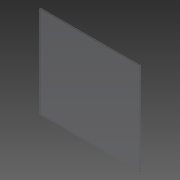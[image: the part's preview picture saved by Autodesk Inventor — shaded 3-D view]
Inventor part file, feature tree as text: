
AUTODESK INVENTOR PART (.ipt)
format: ipt  version: 2013 (Build 170138000, 138)  size: 145,920 bytes
history: native  units: in
note: dims shown in document units (in); Inventor stores cm internally (conversion verified against a paired STEP export)
features: sheet_metal_op x7, other x4, sketch x3
ambient origin geometry x8: Origin, YZ Plane, XZ Plane, XY Plane, X Axis, Y Axis, Z Axis, Center Point
bodies: Solid1 (feature_tree)
feature tree (14):
  sheet_metal_op  "Face1"
  sheet_metal_op  "Flange1"
  sheet_metal_op  "Flange2"
  sketch  "Sketch1"  dims[d0=53.0in]
  other  "Plate1"
  sketch  "Sketch2"  dims[d1=48.0in]
  other  "Plate2"
  sheet_metal_op  "Bend1"
  sheet_metal_op  "Corner1"
  sketch  "Sketch3"  dims[d2=0.12in d3=0.12in d4=0.06in d5=0.24in d6=0.12in d7=1.0in d8=90.0deg d9=0.12in d10=0.48in d11=0.12in d12=0.12in d13=0.12in d14=0.06in d15=0.24in d16=0.12in d17=26.5in d18=90.0deg d19=0.12in d20=0.48in d21=0.12in d22=0.12in]
  other  "Plate3"
  sheet_metal_op  "Bend2"
  sheet_metal_op  "Corner2"
  other  "Definition1"
